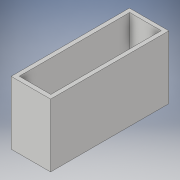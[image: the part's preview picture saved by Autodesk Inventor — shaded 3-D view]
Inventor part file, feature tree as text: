
AUTODESK INVENTOR PART (.ipt)
format: ipt  version: 2019 (Build 230136000, 136)  size: 103,424 bytes
history: native  units: mm
features: extrude x3, sketch x3
ambient origin geometry x8: Origin, YZ Plane, XZ Plane, XY Plane, X Axis, Y Axis, Z Axis, Center Point
bodies: Solid1 (feature_tree)
feature tree (6):
  extrude  "Extrusion1"  Depth=300.0mm
  extrude  "Extrusion2"  Depth=50.0mm
  extrude  "Extrusion3"  Depth=70.0mm TaperAngle=0.0deg
  sketch  "Sketch1"  dims[d0=50.0mm d1=300.0mm]
  sketch  "Sketch2"  dims[d2=80.0mm d3=0.0mm d4=50.0mm]
  sketch  "Sketch3"  dims[d5=150.0mm d6=100.0mm d7=0.0mm d8=40.0mm d9=140.0mm d10=70.0mm d11=0.0mm]
